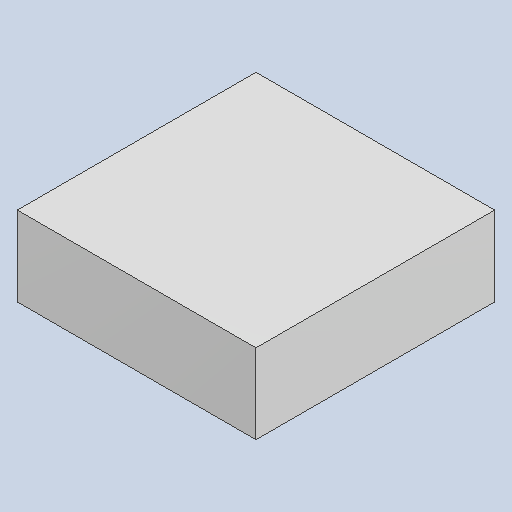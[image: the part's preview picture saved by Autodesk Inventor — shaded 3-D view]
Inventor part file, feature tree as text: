
AUTODESK INVENTOR PART (.ipt)
format: ipt  version: 2023.4 (Build 274418000, 418)  size: 79,872 bytes
history: native  units: mm
features: extrude x1
ambient origin geometry x8: Origin, YZ Plane, XZ Plane, XY Plane, X Axis, Y Axis, Z Axis, Center Point
bodies: Solid1 (feature_tree)
feature tree (1):
  extrude  "Extruded_62"  [1 undecoded]
note: 1 required parameter value undecoded (feature->parameter linkage not recoverable at this tier; creation-order binding heuristic only, values carry confidence <= 0.55)
